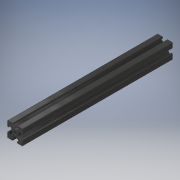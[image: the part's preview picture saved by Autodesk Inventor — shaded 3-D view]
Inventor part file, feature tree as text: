
AUTODESK INVENTOR PART (.ipt)
format: ipt  version: 2019 (Build 230136000, 136)  size: 236,544 bytes
history: native  units: in
note: dims shown in document units (in); Inventor stores cm internally (conversion verified against a paired STEP export)
features: fillet x2, thread x2, extrude x1, sketch x1
ambient origin geometry x8: Origin, YZ Plane, XZ Plane, XY Plane, X Axis, Y Axis, Z Axis, Center Point
bodies: Solid1 (feature_tree)
feature tree (6):
  extrude  "Extrusion1"  Depth=0.3937in
  fillet  "Fillet1"  Radius=0.1378in
  fillet  "Fillet2"  Radius=0.0394in
  thread  "Thread1"  [1 undecoded]
  thread  "Thread2"  [1 undecoded]
  sketch  "Sketch1"  dims[d0=0.0984in d1=0.3937in d2=0.3937in d3=0.1378in d4=0.0394in d5=90.0deg d6=0.1378in d10=0.0787in d11=0.2749in d13=0.3436in d14=0.0394in d15=1.5748in d17=360.0deg d19=0.1225in d21=3.937in d22=0.0in d23=0.0071in d24=0.0118in d25=0.315in d26=0.0in d27=0.315in d28=0.0in]
note: 2 required parameter values undecoded (feature->parameter linkage not recoverable at this tier; creation-order binding heuristic only, values carry confidence <= 0.55)
